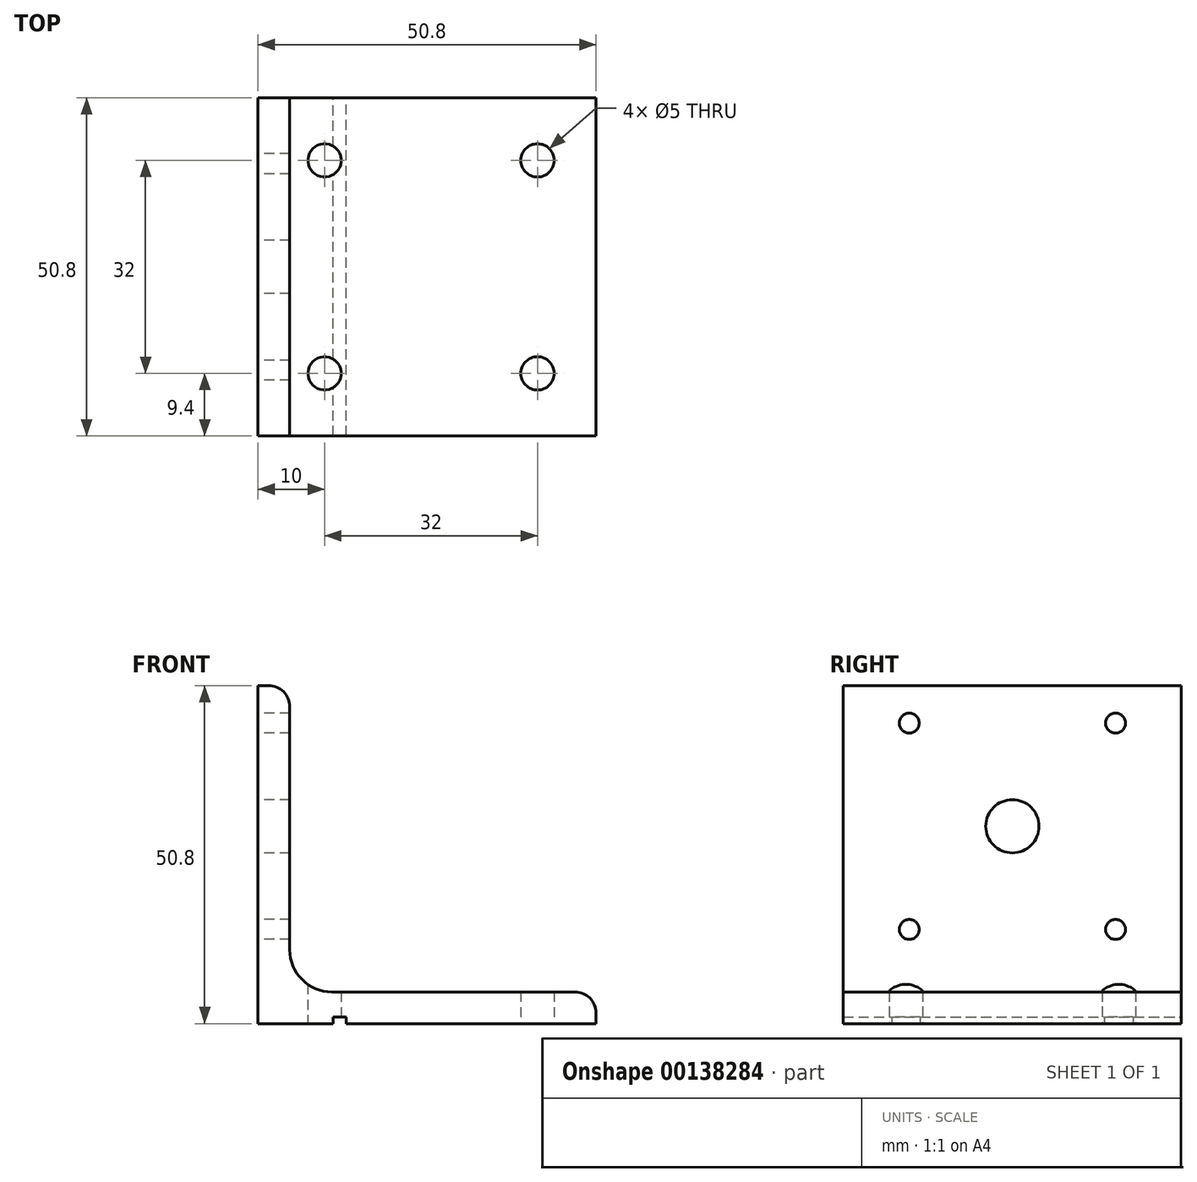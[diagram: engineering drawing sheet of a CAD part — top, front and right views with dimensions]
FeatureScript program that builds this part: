
annotation { "Feature Type Name" : "Feature", "Feature Type Description" : "" }
export const myFeature = defineFeature(function(context is Context, id is Id, definition is map)
    precondition{}
    {
        {
            var Q0;
            Q0=qCreatedBy(makeId("Front.planeOp"),FACE);
            var sketch = newSketch(context, id + "F0", { "sketchPlane" : qUnion([Q0])});
            skLineSegment(sketch, "E0", {"start": v(0, 50.8) * mm, "end": v(0, 0) * mm});
            skLineSegment(sketch, "E1", {"start": v(0, 0) * mm, "end": v(50.8, 0) * mm});
            skLineSegment(sketch, "E2.0", {"start": v(4.76, 4.76) * mm, "end": v(50.8, 4.76) * mm});
            skLineSegment(sketch, "E2.1", {"start": v(4.76, 50.8) * mm, "end": v(4.76, 4.76) * mm});
            skLineSegment(sketch, "E3", {"start": v(0, 50.8) * mm, "end": v(4.76, 50.8) * mm});
            skLineSegment(sketch, "E4", {"start": v(50.8, 0) * mm, "end": v(50.8, 4.76) * mm});
            skSolve(sketch);
        }
        {
            var Q0;
            Q0=makeQuery(id+"F0.imprint","IMPRINT",FACE,{"disambiguationData":[TD([[makeQuery(id+"F0.imprint","IMPRINT",EDGE,{"derivedFrom":sQuery(id+"F0.wireOp",EDGE,"E0")}),1.0]])]});
            extrude(context, id + "F1", {"entities" : qUnion([Q0]), "endBound" : BoundingType.SYMMETRIC, "depth" : 50.8 * mm});
        }
        {
            var Q0;
            Q0=makeQuery(id+"F1.opExtrude","SWEPT_EDGE",EDGE,{"disambiguationData":[OSD([sQuery(id+"F0.wireOp",EDGE,"E2.1"),sQuery(id+"F0.wireOp",EDGE,"E3")])]});
            var Q1;
            Q1=makeQuery(id+"F1.opExtrude","SWEPT_EDGE",EDGE,{"disambiguationData":[OSD([sQuery(id+"F0.wireOp",EDGE,"E2.0"),sQuery(id+"F0.wireOp",EDGE,"E4")])]});
            fillet(context, id + "F2", {"entities" : qUnion([Q0, Q1]), "radius" : 3.17 * mm, "tangentPropagation" : true, "allowEdgeOverflow" : false});
        }
        {
            var Q0;
            Q0=makeQuery(id+"F1.opExtrude","SWEPT_EDGE",EDGE,{"disambiguationData":[OSD([sQuery(id+"F0.wireOp",EDGE,"E2.0"),sQuery(id+"F0.wireOp",EDGE,"E2.1")])]});
            fillet(context, id + "F3", {"entities" : qUnion([Q0]), "radius" : 6.35 * mm, "tangentPropagation" : true, "allowEdgeOverflow" : false});
        }
        {
            var Q0;
            Q0=makeQuery(id+"F1.opExtrude","SWEPT_FACE",FACE,{"disambiguationData":[OSD([sQuery(id+"F0.wireOp",EDGE,"E1")])]});
            var sketch = newSketch(context, id + "F4", { "sketchPlane" : qUnion([Q0])});
            skLineSegment(sketch, "E5.0.0", {"start": v(0, -25.4) * mm, "end": v(50.8, -25.4) * mm, "construction": true});
            skLineSegment(sketch, "E5.0.1", {"start": v(50.8, -25.4) * mm, "end": v(50.8, 25.4) * mm, "construction": true});
            skLineSegment(sketch, "E5.0.2", {"start": v(50.8, 25.4) * mm, "end": v(0, 25.4) * mm, "construction": true});
            skLineSegment(sketch, "E5.0.3", {"start": v(0, 25.4) * mm, "end": v(0, -25.4) * mm, "construction": true});
            skLineSegment(sketch, "E6.bottom", {"start": v(42, 16) * mm, "end": v(10, 16) * mm, "construction": true});
            skLineSegment(sketch, "E6.top", {"start": v(42, -16) * mm, "end": v(10, -16) * mm, "construction": true});
            skLineSegment(sketch, "E6.left", {"start": v(42, 16) * mm, "end": v(42, -16) * mm, "construction": true});
            skLineSegment(sketch, "E6.right", {"start": v(10, 16) * mm, "end": v(10, -16) * mm, "construction": true});
            skPoint(sketch, "E6.middle", {"position": v(26, 0) * mm});
            skPoint(sketch, "E6.middle.positionSnap0", {"position": v(25.4, 25.4) * mm});
            skPoint(sketch, "E6.centerSnap0", {"position": v(25.4, 25.4) * mm});
            skCircle(sketch, "E7", {"center": v(10, 16) * mm, "radius": 2.5 * mm});
            skCircle(sketch, "E8", {"center": v(42, 16) * mm, "radius": 2.5 * mm});
            skCircle(sketch, "E9", {"center": v(42, -16) * mm, "radius": 2.5 * mm});
            skCircle(sketch, "E10", {"center": v(10, -16) * mm, "radius": 2.5 * mm});
            skSolve(sketch);
        }
        {
            var Q0;
            Q0=makeQuery(id+"F4.imprint","IMPRINT",FACE,{"disambiguationData":[TD([[makeQuery(id+"F4.imprint","IMPRINT",EDGE,{"derivedFrom":sQuery(id+"F4.wireOp",EDGE,"E7")}),1.0]])]});
            var Q1;
            Q1=makeQuery(id+"F4.imprint","IMPRINT",FACE,{"disambiguationData":[TD([[makeQuery(id+"F4.imprint","IMPRINT",EDGE,{"derivedFrom":sQuery(id+"F4.wireOp",EDGE,"E8")}),1.0]])]});
            var Q2;
            Q2=makeQuery(id+"F4.imprint","IMPRINT",FACE,{"disambiguationData":[TD([[makeQuery(id+"F4.imprint","IMPRINT",EDGE,{"derivedFrom":sQuery(id+"F4.wireOp",EDGE,"E9")}),1.0]])]});
            var Q3;
            Q3=makeQuery(id+"F4.imprint","IMPRINT",FACE,{"disambiguationData":[TD([[makeQuery(id+"F4.imprint","IMPRINT",EDGE,{"derivedFrom":sQuery(id+"F4.wireOp",EDGE,"E10")}),1.0]])]});
            extrude(context, id + "F5", {"entities" : qUnion([Q0, Q1, Q2, Q3]), "operationType" : NewBodyOperationType.REMOVE, "endBound" : BoundingType.THROUGH_ALL, "oppositeDirection" : true, "depth" : 25 * mm});
        }
        {
            var Q0;
            Q0=makeQuery(id+"F1.opExtrude","SWEPT_FACE",FACE,{"disambiguationData":[OSD([sQuery(id+"F0.wireOp",EDGE,"E0")])]});
            var sketch = newSketch(context, id + "F6", { "sketchPlane" : qUnion([Q0])});
            skLineSegment(sketch, "E11.0.0", {"start": v(-25.4, 50.8) * mm, "end": v(-25.4, 0) * mm, "construction": true});
            skLineSegment(sketch, "E11.0.1", {"start": v(-25.4, 0) * mm, "end": v(25.4, 0) * mm, "construction": true});
            skLineSegment(sketch, "E11.0.2", {"start": v(25.4, 0) * mm, "end": v(25.4, 50.8) * mm, "construction": true});
            skLineSegment(sketch, "E11.0.3", {"start": v(25.4, 50.8) * mm, "end": v(-25.4, 50.8) * mm, "construction": true});
            skLineSegment(sketch, "E12.bottom", {"start": v(15.5, 14.15) * mm, "end": v(-15.5, 14.15) * mm, "construction": true});
            skLineSegment(sketch, "E12.top", {"start": v(15.5, 45.15) * mm, "end": v(-15.5, 45.15) * mm, "construction": true});
            skLineSegment(sketch, "E12.left", {"start": v(15.5, 14.15) * mm, "end": v(15.5, 45.15) * mm, "construction": true});
            skLineSegment(sketch, "E12.right", {"start": v(-15.5, 14.15) * mm, "end": v(-15.5, 45.15) * mm, "construction": true});
            skPoint(sketch, "E12.middle", {"position": v(0, 29.65) * mm});
            skLineSegment(sketch, "E13.bottom", {"start": v(21.15, 50.8) * mm, "end": v(-21.15, 50.8) * mm, "construction": true});
            skLineSegment(sketch, "E13.top", {"start": v(21.15, 8.5) * mm, "end": v(-21.15, 8.5) * mm, "construction": true});
            skLineSegment(sketch, "E13.left", {"start": v(21.15, 50.8) * mm, "end": v(21.15, 8.5) * mm, "construction": true});
            skLineSegment(sketch, "E13.right", {"start": v(-21.15, 50.8) * mm, "end": v(-21.15, 8.5) * mm, "construction": true});
            skCircle(sketch, "E14", {"center": v(15.5, 45.15) * mm, "radius": 1.5 * mm});
            skCircle(sketch, "E15", {"center": v(15.5, 14.15) * mm, "radius": 1.5 * mm});
            skCircle(sketch, "E16", {"center": v(-15.5, 14.15) * mm, "radius": 1.5 * mm});
            skCircle(sketch, "E17", {"center": v(-15.5, 45.15) * mm, "radius": 1.5 * mm});
            skCircle(sketch, "E18", {"center": v(0, 29.65) * mm, "radius": 4 * mm});
            skSolve(sketch);
        }
        {
            var Q0;
            Q0=makeQuery(id+"F6.imprint","IMPRINT",FACE,{"disambiguationData":[TD([[makeQuery(id+"F6.imprint","IMPRINT",EDGE,{"derivedFrom":sQuery(id+"F6.wireOp",EDGE,"E14")}),1.0]])]});
            var Q1;
            Q1=makeQuery(id+"F6.imprint","IMPRINT",FACE,{"disambiguationData":[TD([[makeQuery(id+"F6.imprint","IMPRINT",EDGE,{"derivedFrom":sQuery(id+"F6.wireOp",EDGE,"E15")}),1.0]])]});
            var Q2;
            Q2=makeQuery(id+"F6.imprint","IMPRINT",FACE,{"disambiguationData":[TD([[makeQuery(id+"F6.imprint","IMPRINT",EDGE,{"derivedFrom":sQuery(id+"F6.wireOp",EDGE,"E16")}),1.0]])]});
            var Q3;
            Q3=makeQuery(id+"F6.imprint","IMPRINT",FACE,{"disambiguationData":[TD([[makeQuery(id+"F6.imprint","IMPRINT",EDGE,{"derivedFrom":sQuery(id+"F6.wireOp",EDGE,"E17")}),1.0]])]});
            var Q4;
            Q4=makeQuery(id+"F6.imprint","IMPRINT",FACE,{"disambiguationData":[TD([[makeQuery(id+"F6.imprint","IMPRINT",EDGE,{"derivedFrom":sQuery(id+"F6.wireOp",EDGE,"E18")}),1.0]])]});
            extrude(context, id + "F7", {"entities" : qUnion([Q0, Q1, Q2, Q3, Q4]), "operationType" : NewBodyOperationType.REMOVE, "endBound" : BoundingType.THROUGH_ALL, "oppositeDirection" : true, "depth" : 25 * mm});
        }
        {
            var Q0;
            Q0=makeQuery(id+"F1.opExtrude","SWEPT_FACE",FACE,{"disambiguationData":[OSD([sQuery(id+"F0.wireOp",EDGE,"E1")])]});
            var sketch = newSketch(context, id + "F8", { "sketchPlane" : qUnion([Q0])});
            skLineSegment(sketch, "E19", {"start": v(12.26, 25.4) * mm, "end": v(12.26, -25.4) * mm, "construction": true});
            skLineSegment(sketch, "E20.bottom", {"start": v(13.26, 25.4) * mm, "end": v(11.26, 25.4) * mm});
            skLineSegment(sketch, "E20.top", {"start": v(13.26, -25.4) * mm, "end": v(11.26, -25.4) * mm});
            skLineSegment(sketch, "E20.left", {"start": v(13.26, 25.4) * mm, "end": v(13.26, -25.4) * mm});
            skLineSegment(sketch, "E20.right", {"start": v(11.26, 25.4) * mm, "end": v(11.26, -25.4) * mm});
            skPoint(sketch, "E20.middle", {"position": v(12.26, 0) * mm});
            skSolve(sketch);
        }
        {
            var Q0;
            {var subQ1=sQuery(id+"F8.wireOp",EDGE,"E20.bottom");Q0=makeQuery(id+"F8.imprint","IMPRINT",FACE,{"disambiguationData":[TD([[makeQuery(id+"F8.imprint","IMPRINT",EDGE,{"derivedFrom":subQ1}),-1.0]])]});}
            extrude(context, id + "F9", {"entities" : qUnion([Q0]), "operationType" : NewBodyOperationType.REMOVE, "oppositeDirection" : true, "depth" : 1 * mm});
        }
    });
